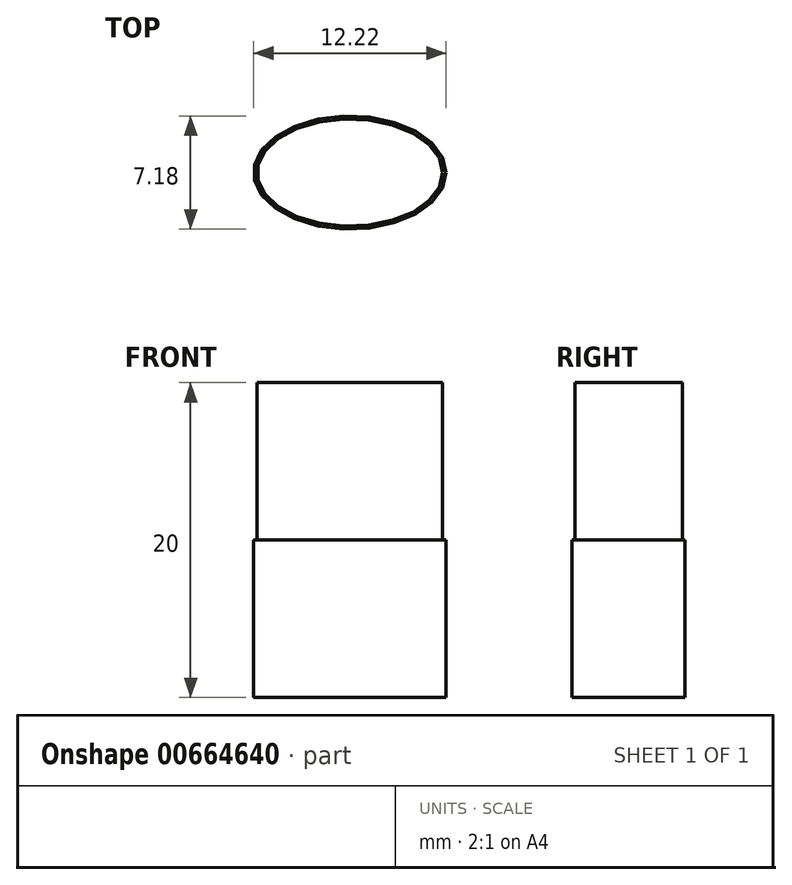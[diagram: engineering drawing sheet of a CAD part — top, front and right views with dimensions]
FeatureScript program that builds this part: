
annotation { "Feature Type Name" : "Feature", "Feature Type Description" : "" }
export const myFeature = defineFeature(function(context is Context, id is Id, definition is map)
    precondition{}
    {
        {
            var Q0;
            Q0=qCreatedBy(makeId("Top.planeOp"),FACE);
            var sketch = newSketch(context, id + "F0", { "sketchPlane" : qUnion([Q0])});
            skEllipse(sketch, "E0", {"center": v(0, 0) * mm, "majorRadius": 6.11 * mm, "minorRadius": 3.59 * mm, "majorAxis": v(1, 0)});
            skSolve(sketch);
        }
        {
            var Q0;
            Q0 = qSketchRegion(id + "F0", true);
            extrude(context, id + "F1", {"entities" : qUnion([Q0]), "depth" : 10 * mm, "offsetDistance" : 25 * mm});
        }
        {
            var Q0;
            Q0=makeQuery(id+"F1.opExtrude","CAP_FACE",FACE,{"disambiguationData":[OSD([sQuery(id+"F0.wireOp",EDGE,"E0")])],"isStart":false});
            var sketch = newSketch(context, id + "F2", { "sketchPlane" : qUnion([Q0])});
            skEllipse(sketch, "E1", {"center": v(0, 0) * mm, "majorRadius": 5.89 * mm, "minorRadius": 3.41 * mm, "majorAxis": v(1, 0)});
            skSolve(sketch);
        }
        {
            var Q0;
            Q0 = qSketchRegion(id + "F2", true);
            extrude(context, id + "F3", {"entities" : qUnion([Q0]), "operationType" : NewBodyOperationType.ADD, "depth" : 10 * mm, "offsetDistance" : 25 * mm});
        }
    });
